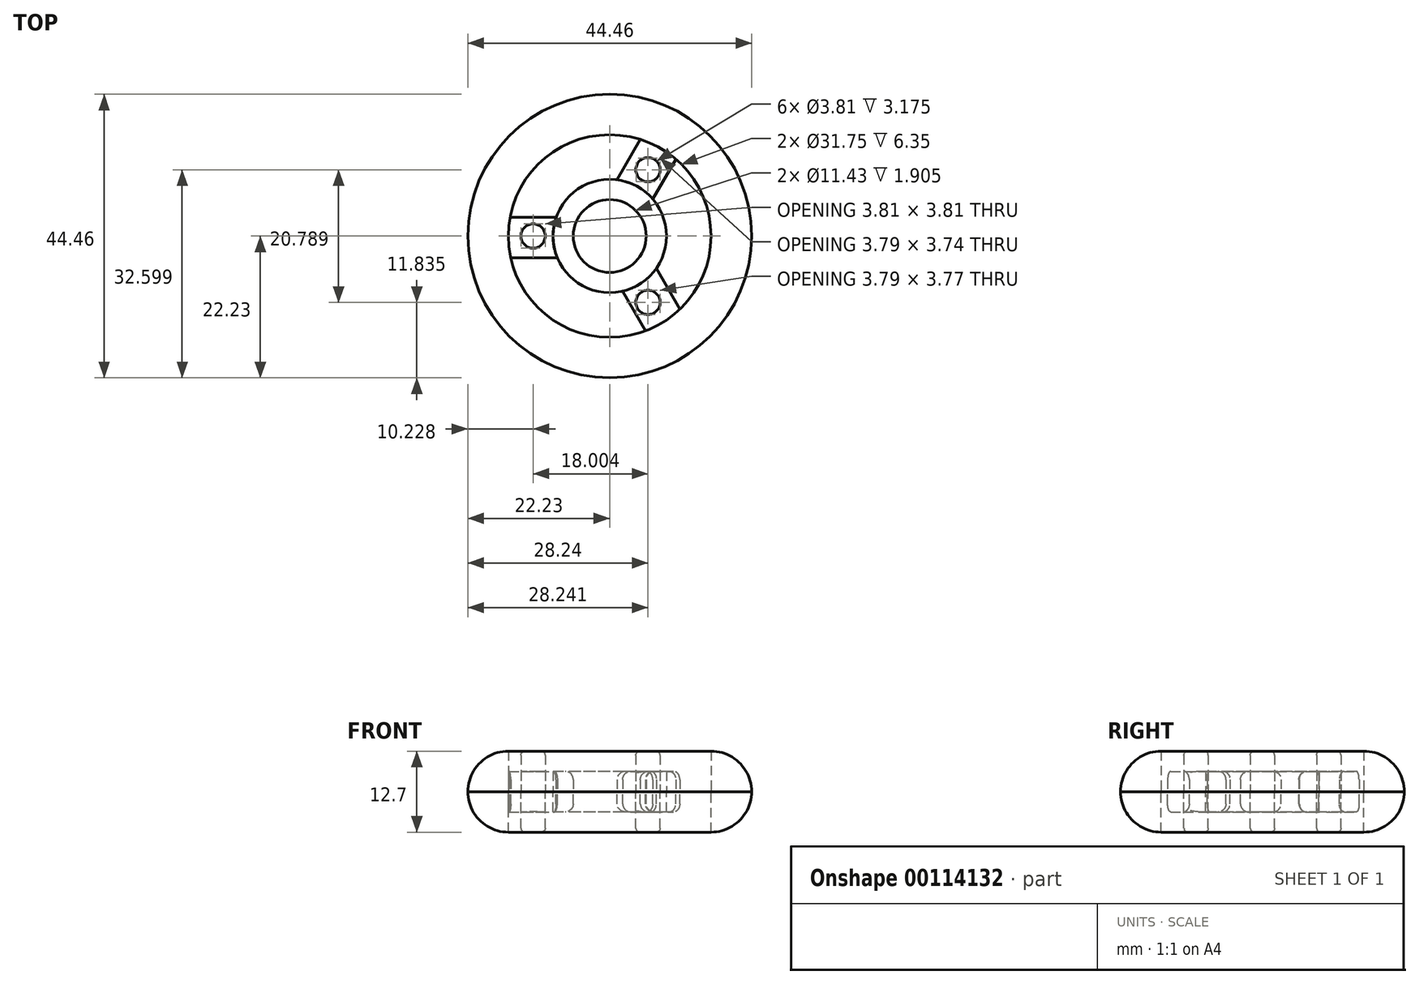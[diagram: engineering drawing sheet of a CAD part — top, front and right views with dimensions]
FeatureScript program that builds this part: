
annotation { "Feature Type Name" : "Feature", "Feature Type Description" : "" }
export const myFeature = defineFeature(function(context is Context, id is Id, definition is map)
    precondition{}
    {
        {
            var Q0;
            Q0=qCreatedBy(makeId("Top.planeOp"),FACE);
            var sketch = newSketch(context, id + "F0", { "sketchPlane" : qUnion([Q0])});
            skCircle(sketch, "E0", {"center": v(0, 0) * mm, "radius": 22.23 * mm});
            skCircle(sketch, "E1", {"center": v(0, 0) * mm, "radius": 5.72 * mm});
            skCircle(sketch, "E2", {"center": v(0, 0) * mm, "radius": 15.88 * mm});
            skLineSegment(sketch, "E3.left", {"start": v(-15.88, 0) * mm, "end": v(-15.88, 0) * mm});
            skLineSegment(sketch, "E3.right", {"start": v(-5.72, 0) * mm, "end": v(-5.72, 0) * mm});
            skLineSegment(sketch, "E4.rect.bottom", {"start": v(-15.6, 2.91) * mm, "end": v(-8.4, 2.91) * mm});
            skLineSegment(sketch, "E4.rect.top", {"start": v(-20.22, -3.44) * mm, "end": v(-8.2, -3.44) * mm});
            skLineSegment(sketch, "E5.1.0", {"start": v(13.5, -15.82) * mm, "end": v(7.3, -5.08) * mm});
            skLineSegment(sketch, "E5.1.1", {"start": v(5.7, -15) * mm, "end": v(2.03, -8.66) * mm});
            skLineSegment(sketch, "E5.2.0", {"start": v(7.36, 19.58) * mm, "end": v(1.15, 8.82) * mm});
            skLineSegment(sketch, "E5.2.1", {"start": v(10.55, 12.4) * mm, "end": v(6.74, 5.8) * mm});
            skPoint(sketch, "E5.center", {"position": v(0.21, 0.1) * mm});
            skCircle(sketch, "E6.0", {"center": v(0, 0) * mm, "radius": 8.9 * mm});
            skPoint(sketch, "E7.orphan", {"position": v(-4.92, 2.91) * mm});
            skPoint(sketch, "E8.orphan", {"position": v(-4.57, -3.44) * mm});
            skPoint(sketch, "E9.orphan", {"position": v(0.35, -5.74) * mm});
            skPoint(sketch, "E10.orphan", {"position": v(5.67, -2.26) * mm});
            skPoint(sketch, "E11.orphan", {"position": v(5.2, 3.15) * mm});
            skPoint(sketch, "E12.orphan", {"position": v(-0.47, 6.02) * mm});
            skCircle(sketch, "E13", {"center": v(-12, 0) * mm, "radius": 1.9 * mm});
            skPoint(sketch, "E13.centerSnap0", {"position": v(-12, 2.91) * mm});
            skCircle(sketch, "E14.1.0", {"center": v(6, -10.4) * mm, "radius": 1.9 * mm});
            skCircle(sketch, "E14.2.0", {"center": v(6, 10.4) * mm, "radius": 1.9 * mm});
            skSolve(sketch);
        }
        {
            var Q0;
            {var subQ5=sQuery(id+"F0.wireOp",EDGE,"E4.rect.bottom");Q0=makeQuery(id+"F0.imprint","IMPRINT",FACE,{"disambiguationData":[TD([[makeQuery(id+"F0.imprint","IMPRINT",EDGE,{"derivedFrom":subQ5}),-1.0]])]});}
            var Q1;
            {var subQ0=sQuery(id+"F0.wireOp",EDGE,"E5.1.1");Q1=makeQuery(id+"F0.imprint","IMPRINT",FACE,{"disambiguationData":[TD([[makeQuery(id+"F0.imprint","IMPRINT",EDGE,{"derivedFrom":subQ0}),-1.0]])]});}
            var Q2;
            {var subQ5=sQuery(id+"F0.wireOp",EDGE,"E5.2.1");Q2=makeQuery(id+"F0.imprint","IMPRINT",FACE,{"disambiguationData":[TD([[makeQuery(id+"F0.imprint","IMPRINT",EDGE,{"derivedFrom":subQ5}),-1.0]])]});}
            extrude(context, id + "F1", {"entities" : qUnion([Q0, Q1, Q2]), "depth" : 3.17 * mm});
        }
        {
            var Q0;
            Q0=makeQuery(id+"F0.imprint","IMPRINT",FACE,{"disambiguationData":[TD([[makeQuery(id+"F0.imprint","IMPRINT",EDGE,{"derivedFrom":sQuery(id+"F0.wireOp",EDGE,"E13")}),1.0]])]});
            var Q1;
            Q1=makeQuery(id+"F0.imprint","IMPRINT",FACE,{"disambiguationData":[TD([[makeQuery(id+"F0.imprint","IMPRINT",EDGE,{"derivedFrom":sQuery(id+"F0.wireOp",EDGE,"E14.2.0")}),1.0]])]});
            var Q2;
            Q2=makeQuery(id+"F0.imprint","IMPRINT",FACE,{"disambiguationData":[TD([[makeQuery(id+"F0.imprint","IMPRINT",EDGE,{"derivedFrom":sQuery(id+"F0.wireOp",EDGE,"E14.1.0")}),1.0]])]});
            extrude(context, id + "F2", {"entities" : qUnion([Q0, Q1, Q2]), "depth" : 6.35 * mm});
        }
        {
            var Q0;
            Q0=makeQuery(id+"F0.imprint","IMPRINT",FACE,{"disambiguationData":[TD([[makeQuery(id+"F0.imprint","IMPRINT",EDGE,{"derivedFrom":sQuery(id+"F0.wireOp",EDGE,"E1")}),-1.0]])]});
            extrude(context, id + "F3", {"entities" : qUnion([Q0]), "depth" : 3.17 * mm});
        }
        {
            var Q0;
            Q0=makeQuery(id+"F0.imprint","IMPRINT",FACE,{"disambiguationData":[TD([[makeQuery(id+"F0.imprint","IMPRINT",EDGE,{"derivedFrom":sQuery(id+"F0.wireOp",EDGE,"E0")}),1.0]])]});
            extrude(context, id + "F4", {"entities" : qUnion([Q0]), "depth" : 6.35 * mm});
        }
        {
            var Q0;
            Q0=makeQuery(id+"F4.opExtrude","CAP_EDGE",EDGE,{"disambiguationData":[OSD([sQuery(id+"F0.wireOp",EDGE,"E0")])],"isStart":false});
            fillet(context, id + "F5", {"entities" : qUnion([Q0]), "radius" : 6.35 * mm, "tangentPropagation" : true, "allowEdgeOverflow" : false});
        }
        {
            var Q0;
            Q0=makeQuery(id+"F2.opExtrude","CAP_EDGE",EDGE,{"disambiguationData":[OSD([sQuery(id+"F0.wireOp",EDGE,"E14.1.0")])],"isStart":false});
            var Q1;
            Q1=makeQuery(id+"F2.opExtrude","CAP_EDGE",EDGE,{"disambiguationData":[OSD([sQuery(id+"F0.wireOp",EDGE,"E13")])],"isStart":false});
            var Q2;
            Q2=makeQuery(id+"F2.opExtrude","CAP_EDGE",EDGE,{"disambiguationData":[OSD([sQuery(id+"F0.wireOp",EDGE,"E14.2.0")])],"isStart":false});
            fillet(context, id + "F6", {"entities" : qUnion([Q0, Q1, Q2]), "radius" : 0.64 * mm, "tangentPropagation" : true, "allowEdgeOverflow" : false});
        }
        {
            var Q0;
            Q0=makeQuery(id+"F3.opExtrude","CAP_EDGE",EDGE,{"disambiguationData":[OSD([sQuery(id+"F0.wireOp",EDGE,"E1")])],"isStart":false});
            fillet(context, id + "F7", {"entities" : qUnion([Q0]), "radius" : 1.27 * mm, "tangentPropagation" : true, "allowEdgeOverflow" : false});
        }
        {
            var Q0;
            Q0=makeQuery(id+"F1.opExtrude","CAP_EDGE",EDGE,{"disambiguationData":[OSD([sQuery(id+"F0.wireOp",EDGE,"E5.2.1")])],"isStart":false});
            var Q1;
            Q1=makeQuery(id+"F1.opExtrude","CAP_EDGE",EDGE,{"disambiguationData":[OSD([sQuery(id+"F0.wireOp",EDGE,"E5.1.0")])],"isStart":false});
            var Q2;
            Q2=makeQuery(id+"F1.opExtrude","CAP_EDGE",EDGE,{"disambiguationData":[OSD([sQuery(id+"F0.wireOp",EDGE,"E5.1.1")])],"isStart":false});
            var Q3;
            Q3=makeQuery(id+"F1.opExtrude","CAP_EDGE",EDGE,{"disambiguationData":[OSD([sQuery(id+"F0.wireOp",EDGE,"E4.rect.top")])],"isStart":false});
            var Q4;
            Q4=makeQuery(id+"F1.opExtrude","CAP_EDGE",EDGE,{"disambiguationData":[OSD([sQuery(id+"F0.wireOp",EDGE,"E4.rect.bottom")])],"isStart":false});
            var Q5;
            Q5=makeQuery(id+"F1.opExtrude","CAP_EDGE",EDGE,{"disambiguationData":[OSD([sQuery(id+"F0.wireOp",EDGE,"E5.2.0")])],"isStart":false});
            fillet(context, id + "F8", {"entities" : qUnion([Q0, Q1, Q2, Q3, Q4, Q5]), "radius" : 1.27 * mm, "tangentPropagation" : true, "allowEdgeOverflow" : false});
        }
        {
            var Q0;
            Q0=makeQuery(id+"F4.opExtrude","SWEPT_BODY",BODY,{"disambiguationData":[OSD([sQuery(id+"F0.wireOp",EDGE,"E0"),sQuery(id+"F0.wireOp",EDGE,"E2")])]});
            var Q1;
            Q1=makeQuery(id+"F3.opExtrude","SWEPT_BODY",BODY,{"disambiguationData":[OSD([sQuery(id+"F0.wireOp",EDGE,"E1"),sQuery(id+"F0.wireOp",EDGE,"E6.0")])]});
            var Q2;
            Q2=makeQuery(id+"F2.opExtrude","SWEPT_BODY",BODY,{"disambiguationData":[OSD([sQuery(id+"F0.wireOp",EDGE,"E13")])]});
            var Q3;
            Q3=makeQuery(id+"F1.opExtrude","SWEPT_BODY",BODY,{"disambiguationData":[OSD([sQuery(id+"F0.wireOp",EDGE,"E2"),sQuery(id+"F0.wireOp",EDGE,"E4.rect.bottom"),sQuery(id+"F0.wireOp",EDGE,"E4.rect.top"),sQuery(id+"F0.wireOp",EDGE,"E6.0"),sQuery(id+"F0.wireOp",EDGE,"E13")])]});
            var Q4;
            Q4=makeQuery(id+"F2.opExtrude","SWEPT_BODY",BODY,{"disambiguationData":[OSD([sQuery(id+"F0.wireOp",EDGE,"E14.2.0")])]});
            var Q5;
            Q5=makeQuery(id+"F1.opExtrude","SWEPT_BODY",BODY,{"disambiguationData":[OSD([sQuery(id+"F0.wireOp",EDGE,"E2"),sQuery(id+"F0.wireOp",EDGE,"E5.2.0"),sQuery(id+"F0.wireOp",EDGE,"E5.2.1"),sQuery(id+"F0.wireOp",EDGE,"E6.0"),sQuery(id+"F0.wireOp",EDGE,"E14.2.0")])]});
            var Q6;
            Q6=makeQuery(id+"F1.opExtrude","SWEPT_BODY",BODY,{"disambiguationData":[OSD([sQuery(id+"F0.wireOp",EDGE,"E2"),sQuery(id+"F0.wireOp",EDGE,"E5.1.0"),sQuery(id+"F0.wireOp",EDGE,"E5.1.1"),sQuery(id+"F0.wireOp",EDGE,"E6.0"),sQuery(id+"F0.wireOp",EDGE,"E14.1.0")])]});
            var Q7;
            Q7=makeQuery(id+"F2.opExtrude","SWEPT_BODY",BODY,{"disambiguationData":[OSD([sQuery(id+"F0.wireOp",EDGE,"E14.1.0")])]});
            var Q8;
            Q8=makeQuery(id+"F4.opExtrude","CAP_FACE",FACE,{"disambiguationData":[OSD([sQuery(id+"F0.wireOp",EDGE,"E0"),sQuery(id+"F0.wireOp",EDGE,"E2")])],"isStart":true});
            mirror(context, id + "F9", {"entities" : qUnion([Q0, Q1, Q2, Q3, Q4, Q5, Q6, Q7]), "mirrorPlane" : qUnion([Q8])});
        }
    });
